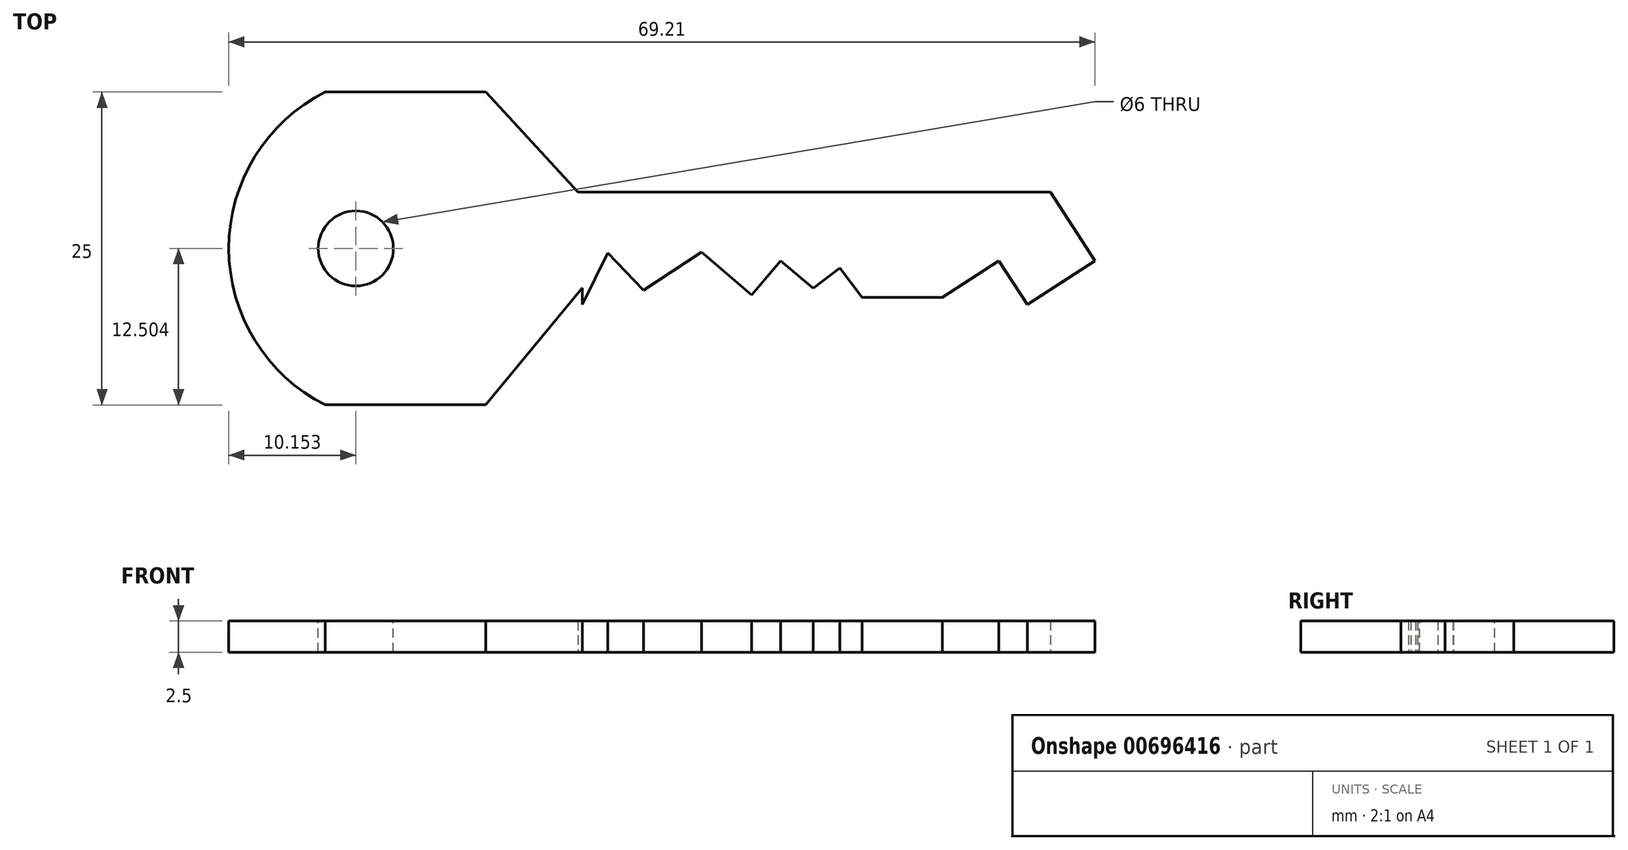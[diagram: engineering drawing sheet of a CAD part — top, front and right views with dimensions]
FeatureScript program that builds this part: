
annotation { "Feature Type Name" : "Feature", "Feature Type Description" : "" }
export const myFeature = defineFeature(function(context is Context, id is Id, definition is map)
    precondition{}
    {
        {
            var Q0;
            Q0=qCreatedBy(makeId("Top.planeOp"),FACE);
            var sketch = newSketch(context, id + "F0", { "sketchPlane" : qUnion([Q0])});
            skLineSegment(sketch, "E0", {"start": v(5.68, 13.48) * mm, "end": v(18.5, 13.48) * mm});
            skLineSegment(sketch, "E1", {"start": v(18.5, 13.48) * mm, "end": v(25.86, 5.48) * mm});
            skLineSegment(sketch, "E2", {"start": v(25.86, 5.48) * mm, "end": v(63.62, 5.48) * mm});
            skLineSegment(sketch, "E3", {"start": v(63.62, 5.48) * mm, "end": v(67.18, 0) * mm});
            skLineSegment(sketch, "E4", {"start": v(67.18, 0) * mm, "end": v(61.77, -3.52) * mm});
            skLineSegment(sketch, "E5", {"start": v(61.77, -3.52) * mm, "end": v(59.48, 0) * mm});
            skLineSegment(sketch, "E6", {"start": v(59.48, 0) * mm, "end": v(54.98, -2.92) * mm});
            skLineSegment(sketch, "E7", {"start": v(54.98, -2.92) * mm, "end": v(48.57, -2.92) * mm});
            skLineSegment(sketch, "E8", {"start": v(48.57, -2.92) * mm, "end": v(46.8, -0.58) * mm});
            skLineSegment(sketch, "E9", {"start": v(46.8, -0.58) * mm, "end": v(44.66, -2.2) * mm});
            skLineSegment(sketch, "E10", {"start": v(44.66, -2.2) * mm, "end": v(42.06, 0) * mm});
            skLineSegment(sketch, "E11", {"start": v(42.06, 0) * mm, "end": v(39.75, -2.72) * mm});
            skLineSegment(sketch, "E12", {"start": v(39.75, -2.72) * mm, "end": v(35.73, 0.68) * mm});
            skLineSegment(sketch, "E13", {"start": v(35.73, 0.68) * mm, "end": v(31.12, -2.35) * mm});
            skLineSegment(sketch, "E14", {"start": v(31.12, -2.35) * mm, "end": v(28.25, 0.64) * mm});
            skLineSegment(sketch, "E15", {"start": v(28.25, 0.64) * mm, "end": v(26.23, -3.52) * mm});
            skLineSegment(sketch, "E16", {"start": v(26.23, -3.52) * mm, "end": v(26.23, -2.18) * mm});
            skLineSegment(sketch, "E17", {"start": v(26.23, -2.18) * mm, "end": v(18.5, -11.52) * mm});
            skLineSegment(sketch, "E18", {"start": v(18.5, -11.52) * mm, "end": v(5.68, -11.52) * mm});
            skArc(sketch, "E19", {"start": v(5.68, 13.48) * mm, "mid": v(-2.03, 0.98) * mm, "end": v(5.68, -11.52) * mm});
            skPoint(sketch, "E20.end.orphan", {"position": v(-5.75, 0) * mm});
            skSolve(sketch);
        }
        {
            var Q0;
            Q0=qSketchRegion(id+"F0",true);
            extrude(context, id + "F1", {"entities" : qUnion([Q0]), "depth" : 2.5 * mm, "offsetDistance" : 25 * mm});
        }
        {
            var Q0;
            Q0=makeQuery(id+"F1.opExtrude","CAP_FACE",FACE,{"disambiguationData":[OSD([sQuery(id+"F0.wireOp",EDGE,"E0"),sQuery(id+"F0.wireOp",EDGE,"E1"),sQuery(id+"F0.wireOp",EDGE,"E2"),sQuery(id+"F0.wireOp",EDGE,"E3"),sQuery(id+"F0.wireOp",EDGE,"E4"),sQuery(id+"F0.wireOp",EDGE,"E5"),sQuery(id+"F0.wireOp",EDGE,"E6"),sQuery(id+"F0.wireOp",EDGE,"E7"),sQuery(id+"F0.wireOp",EDGE,"E8"),sQuery(id+"F0.wireOp",EDGE,"E9"),sQuery(id+"F0.wireOp",EDGE,"E10"),sQuery(id+"F0.wireOp",EDGE,"E11"),sQuery(id+"F0.wireOp",EDGE,"E12"),sQuery(id+"F0.wireOp",EDGE,"E13"),sQuery(id+"F0.wireOp",EDGE,"E14"),sQuery(id+"F0.wireOp",EDGE,"E15"),sQuery(id+"F0.wireOp",EDGE,"E16"),sQuery(id+"F0.wireOp",EDGE,"E17"),sQuery(id+"F0.wireOp",EDGE,"E18"),sQuery(id+"F0.wireOp",EDGE,"E19")])],"isStart":false});
            var sketch = newSketch(context, id + "F2", { "sketchPlane" : qUnion([Q0])});
            skCircle(sketch, "E21", {"center": v(8.12, 0.98) * mm, "radius": 3 * mm});
            skSolve(sketch);
        }
        {
            var Q0;
            Q0=qSketchRegion(id+"F2",true);
            extrude(context, id + "F3", {"entities" : qUnion([Q0]), "operationType" : NewBodyOperationType.REMOVE, "oppositeDirection" : true, "depth" : 25 * mm, "offsetDistance" : 25 * mm});
        }
    });
